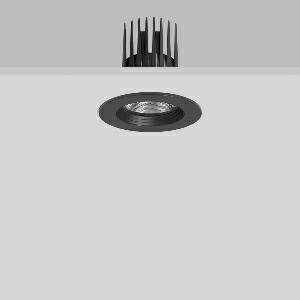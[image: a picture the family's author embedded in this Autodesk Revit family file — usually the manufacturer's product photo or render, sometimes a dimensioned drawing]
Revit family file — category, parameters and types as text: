
# Revit family: heledon_mini_e_901740_003_3_76_9d52
name_source: partatom
category: Lighting Fixtures
units: mm (PartAtom-declared; Revit-internal decimal feet)

## family parameters
Cut with Voids When Loaded = No
Host = Face
Light Source = No
Part Type = Normal
Room Calculation Point = No
Round Connector Dimension = Use Diameter
Shared = No

## types (1)
- HELEDON mini E (1 x LED Modul 935, 2600 lm, 3500)
    Apparent Load = 20 VA
    Approval mark = CE
    CIE Flux Codes = 100 100 100 100 100
    Color Rendering = 92
    Color Temperature = 3500
    Default Elevation = 1800 mm
    Description = Series: HELEDON mini
Round recessed downlight. Housing: die-cast aluminium, powder-coated. Black plastic ring and recessed LED to prevent glare from the side. Optical assembly with reflector made of MIRO-Silver with 98% total light reflection for outstanding efficiency - can be changed without tools. Best colour rendering index Ra>90. Suitable for Recessed ceiling mounting. Installation without tools thanks to spring fastening system. Including separate LED converter with connecting cable 600 mm.High quality converter without flickering and stroboscopic effect. Through-wiring box (5 pole) available as accessory. The following accessories can be mounted without use of tools: interchangeable lenses, decorative glasses, honeycomb louvre, clear and frosted diffusers, white interchangeable plastic ring. 
Colour: deep black, matt (RAL 9005)
Diameter: 124 mm
Height: 3 mm
Cut-out diameter: 114 mm
Recess height: 170 mm
Luminaire: recess height: 120 mm
Lamp: LED
Socket: without socket
Colour temperature: 3500K
Colour rendering index (CRI): 92
System power: 20 W
Rated luminous flux: 2600 lm
Luminous efficiency: 130 lm/W
Control gear: Converter, dimmable, DALI
Protection class: II
Type of protection: IP 20
    Height = 0 mm  [stored 0 ft]
    Lamp = 1 x LED Modul 935
    Lamp Light Flux = 2600 lm
    Lamp count = 1
    Length = 124 mm  [stored 0.406824 ft]
    Lifetime = 50000 h
    Luminous efficacy = 130 lm/W
    Manufacturer = RZB
    ModVariant = No
    Model = 901740.003.3.76
    Mounting Place = Ceiling
    Mounting Type = Recessed
    Number of Poles = 1
    OnlyDefault = Yes
    Power Factor = 1
    Product Name = HELEDON mini E
    Product group = Recessed downlights
    ProductGroupID = 402
    Protection Class = Protection class II
    Protection Degree = IP 20
    RLX_Detail_Level = 1
    RLX_Emergency_Light_Flux = 0 lm
    RLX_Emergency_Type = 0
    RLX_Emergency_Type_DB = No
    RlxData = <blob elided: 126437 chars, md5=9f2abce6>
    Socket = socket
    Standby Power = 0 W
    System Light Flux = 2600 lm
    System Power = 20 W
    Type Comments = Product without accessories
    Type Image = 901657.003.jpg
    URL = http://relux.com
    VarID = ---
    Voltage = 230 V
    Voltage Range = 220-240 V
    Weight = 0.00 kg
    Width = 0 mm  [stored 0 ft]

note: [stored X ft] marks values corroborated as IEEE doubles in the binary element streams (Revit-internal decimal feet)

## geometry (parser evidence)
native form markers: Blend x4, Sweep x12
no freeform markers — native parametric forms only
